# Revit family: MT Model (1)
name_source: partatom
category: Mechanical Equipment
units: mm (PartAtom-declared; Revit-internal decimal feet)

## family parameters
Always vertical = Yes
Cut with Voids When Loaded = Yes
OmniClass Number = 23.40.40.11.17
OmniClass Title = Refrigerated Cases
Part Type = Normal
Room Calculation Point = No
Round Connector Dimension = Use Radius
Shared = No
Work Plane-Based = Yes

## types (1)
- RivaCold CO2 CDU
    10" Shelf = Yes
    Actual Weight = 0
    DATE = 08-April-2021
    DESIGNERS NAME = TAG
    DRAIN LINE = 24"
    DRAIN LINE CONNECTION = SANITARY LINE CONNECTION
    DRAIN LINE DIAMETER = 2"
    DRAIN PIPE TYPE = PVC
    DRAIN PIPING = Yes
    DRIP PAN PLUMB TYPE = HARD
    Default Elevation = 48"
    Defrost Num Day = 0
    Defrost Termination = 0
    Defrost Type = TIMED-OFF DEFROST
    Description = RivaCold CO2 CDU
    EQUIPMENT DESCRIPTION = RivaCold CO2 CDU
    EQUIPMENT MARK = RivaCold CO2 CDU
    Evap Temp = 0
    FAN AMPS = 0 A
    GLASS = Glass
    Height = 57 3/4"
    Item Description = RivaCold CO2 CDU
    LF STD END = Yes
    LIGHT AMPS = 0 A
    LIQUID LINE CONNECTION = LIQUID LINE CONNECTION
    LIQUID LINE DIAMETER = 0"
    LIQUID LINE RADIUS = 0"
    LOAD 1 CLASSIFICATION = Lighting
    LOAD 1 DESCRIPTION = LIGHTING CONNECTION
    LOAD 1 PLUG TYPE = HARDWIRED
    LOAD 1 POLES = 1
    LOAD 1 VOLTAGE = 120 V
    LOAD 1 WATTAGE = 0 W
    LOAD 2 CLASSIFICATION = Motor
    LOAD 2 DESCRIPTION = FAN CONNECTION
    LOAD 2 PLUG TYPE = HARDWIRED
    LOAD 2 POLES = 1
    LOAD 2 VOLTAGE = 120 V
    LOAD 2 WATTAGE = 0 W
    LOAD 3 CLASSIFICATION = Power
    LOAD 3 DESCRIPTION = ANTI-SWEAT CONNECTION
    LOAD 3 PLUG TYPE = HARDWIRED
    LOAD 3 POLES = 1
    LOAD 3 VOLTAGE = 120 V
    LOAD 3 WATTAGE = 0 W
    Legend Number = RivaCold CO2 CDU
    Length = 59 3/8"
    Load Mbh = 0
    Manufacturer = HILL PHOENIX
    Model = RivaCold CO2 CDU
    PAINTED METAL UPPER SHELF = <By Category>
    POWER FACTOR = 0
    PRESSURE REGULATOR = 0.00 psi
    REAR REFRIGERATION PIPING = Yes
    REFRIGERATION PIPING = COPPER PIPE
    RT STD END = Yes
    SANITARY MOUNTING HEIGHT = 0"
    SANITARY PIPE SIZE = 1"
    SELF CONTAINED AMPS = 0 A
    SIZE OF COLD WATER HOOK UP = 0"
    SIZE OF HOT WATER HOOK-UP = 0"
    STAINLESS STEEL = GALVANIZED STEEL
    SUCTION LINE CONNECTION = SUCTION LINE CONNECTION
    SUCTION LINE DIAMETER = 1"
    SUCTION LINE RADIUS = 0"
    TOP ELECTRICAL = Yes
    TOP REFRIGERATION PIPING = Yes
    TOTAL AMPS = 0 A
    URL = http://www.hillphoenix.com
    VOLTS = 0 V
    Width = 20 1/16"

## geometry (parser evidence)
native form markers: Blend x7, Sweep x5
no freeform markers — native parametric forms only
